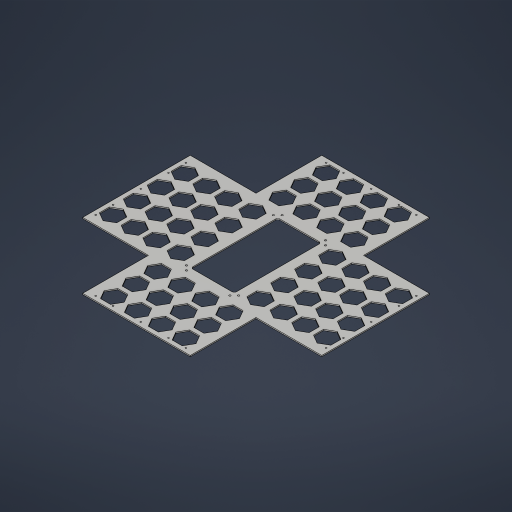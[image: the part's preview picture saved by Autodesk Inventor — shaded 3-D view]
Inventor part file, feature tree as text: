
AUTODESK INVENTOR PART (.ipt)
format: ipt  version: 2023 (Build 270158000, 158)  size: 718,336 bytes
history: native  units: in
note: dims shown in document units (in); Inventor stores cm internally (conversion verified against a paired STEP export)
features: sketch x4, other x2, sheet_metal_op x1, hole x1, chamfer x1
ambient origin geometry x8: Origin, YZ Plane, XZ Plane, XY Plane, X Axis, Y Axis, Z Axis, Center Point
bodies: Solid1 (feature_tree)
feature tree (9):
  parser-record x1  (decoder bookkeeping rows leaked as tree rows — omitted from the tree; the rows remain in map.json)
  sheet_metal_op  "Face1"
  hole  "Hole1"  [1 undecoded]
  sketch  "Sketch3"  dims[d3=0.5in]
  sketch  "Sketch4"  dims[d4=0.5in d5=0.5in d6=0.5in d7=1.0in d8=2.0in d9=1.0in d10=2.0in d11=1.0in d12=2.0in d13=1.0in d14=2.0in d15=0.161in d16=0.75in d17=0.375in d18=0.06in d19=0.5635in d20=0.125in d21=0.8108in d43=5.0in d44=10.0in d45=0.25in d46=0.5in d47=0.5in d48=0.5in d49=0.5in d50=0.5in d51=0.5in d52=0.5in d53=0.5in d54=0.2031in d55=1.0in d56=1.5in d57=2.0in d58=1.5748in d60=2.75in d61=1.1811in d63=2.5in d66=1.5748in d68=360.0deg d70=1.5748in d72=2.75in d73=0.3937in d75=1.0in d77=0.661in]
  chamfer  "Corner Round1"
  sketch  "Sketch1"  dims[d0=27.5in d1=7.5625in]
  other  "Plate1"
  sketch  "Sketch2"  dims[d2=0.125in]
note: 1 required parameter value undecoded (feature->parameter linkage not recoverable at this tier; creation-order binding heuristic only, values carry confidence <= 0.55)
note: 1 file-system path scrubbed to <path> (originals preserved in map.json)
